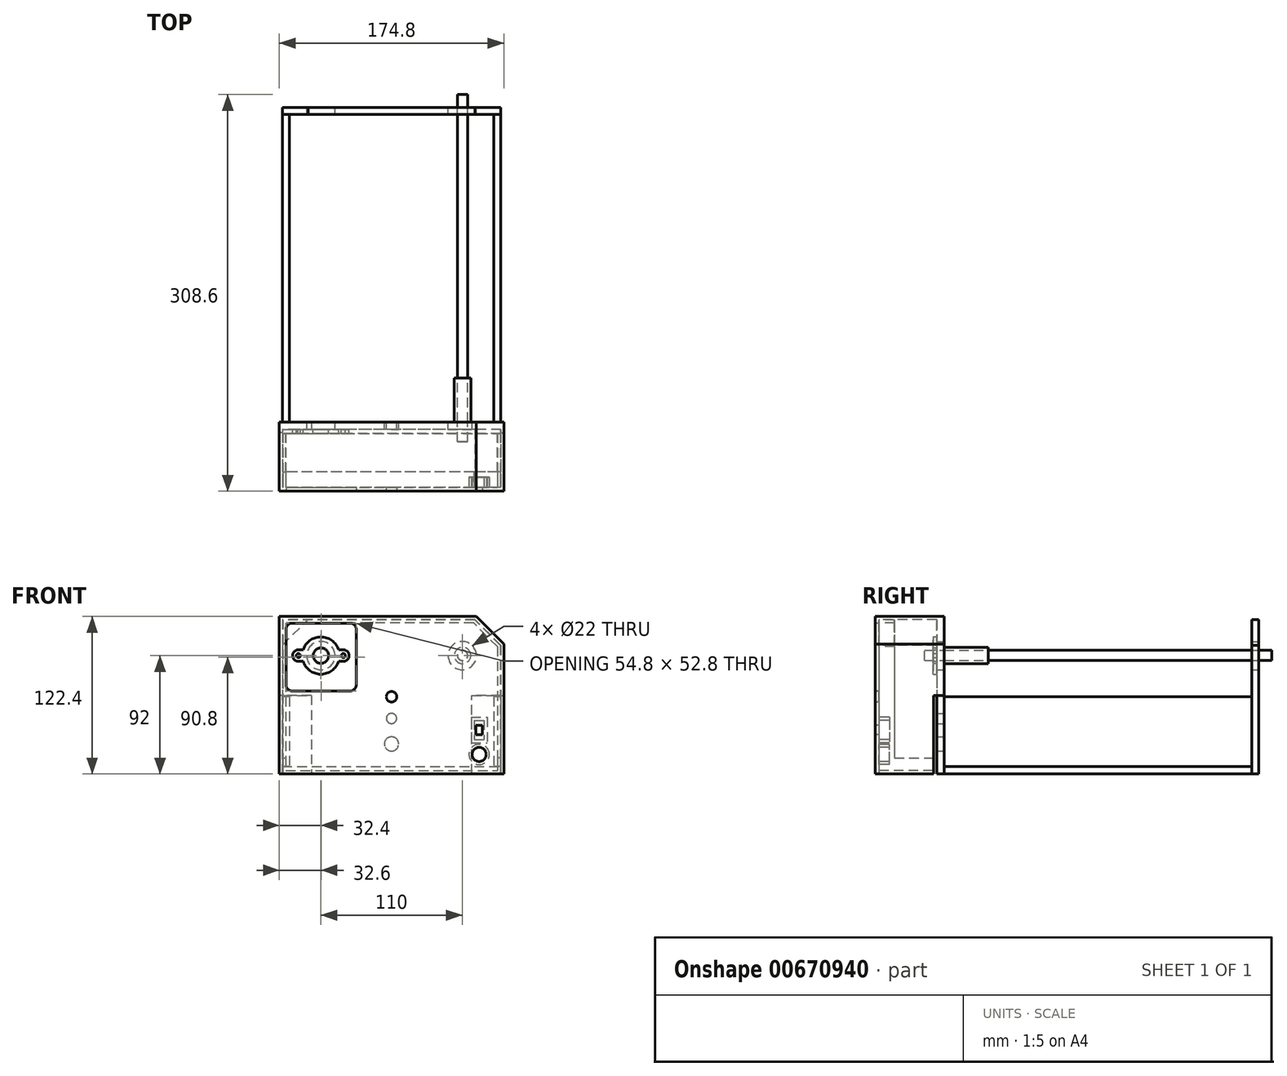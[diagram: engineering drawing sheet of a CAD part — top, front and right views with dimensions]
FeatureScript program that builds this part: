
annotation { "Feature Type Name" : "Feature", "Feature Type Description" : "" }
export const myFeature = defineFeature(function(context is Context, id is Id, definition is map)
    precondition{}
    {
        {
            var Q0;
            Q0=qCreatedBy(makeId("Front.planeOp"),FACE);
            var sketch = newSketch(context, id + "F0", { "sketchPlane" : qUnion([Q0])});
            skLineSegment(sketch, "E0.bottom", {"start": v(85, 60) * mm, "end": v(-85, 60) * mm});
            skLineSegment(sketch, "E0.top", {"start": v(85, -60) * mm, "end": v(-85, -60) * mm});
            skLineSegment(sketch, "E0.left", {"start": v(85, 60) * mm, "end": v(85, -60) * mm});
            skLineSegment(sketch, "E0.right", {"start": v(-85, 60) * mm, "end": v(-85, -60) * mm});
            skPoint(sketch, "E0.middle", {"position": v(0, 0) * mm});
            skLineSegment(sketch, "E1", {"start": v(-85, 32) * mm, "end": v(85, 32) * mm, "construction": true});
            skLineSegment(sketch, "E2", {"start": v(0, 60) * mm, "end": v(0, -60) * mm, "construction": true});
            skLineSegment(sketch, "E3", {"start": v(55, 60) * mm, "end": v(55, -60) * mm, "construction": true});
            skLineSegment(sketch, "E4", {"start": v(-55, 60) * mm, "end": v(-55, -60) * mm, "construction": true});
            skCircle(sketch, "E5", {"center": v(-55, 32) * mm, "radius": 11 * mm});
            skCircle(sketch, "E6", {"center": v(55, 32) * mm, "radius": 11 * mm});
            skSolve(sketch);
        }
        {
            var Q0;
            Q0=makeQuery(id+"F0.imprint","IMPRINT",FACE,{"disambiguationData":[TD([[makeQuery(id+"F0.imprint","IMPRINT",EDGE,{"derivedFrom":sQuery(id+"F0.wireOp",EDGE,"E0.bottom")}),1.0]])]});
            extrude(context, id + "F1", {"entities" : qUnion([Q0]), "depth" : 5.6 * mm, "offsetDistance" : 25 * mm});
        }
        {
            var Q0;
            Q0=makeQuery(id+"F1.opExtrude","SWEPT_EDGE",EDGE,{"disambiguationData":[OSD([sQuery(id+"F0.wireOp",EDGE,"E0.bottom"),sQuery(id+"F0.wireOp",EDGE,"E0.right")])]});
            var Q1;
            Q1=makeQuery(id+"F1.opExtrude","SWEPT_EDGE",EDGE,{"disambiguationData":[OSD([sQuery(id+"F0.wireOp",EDGE,"E0.bottom"),sQuery(id+"F0.wireOp",EDGE,"E0.left")])]});
            chamfer(context, id + "F2", {"entities" : qUnion([Q0, Q1]), "width" : 20 * mm, "tangentPropagation" : true});
        }
        {
            var Q0;
            Q0=makeQuery(id+"F1.opExtrude","SWEPT_BODY",BODY,{"disambiguationData":[OSD([sQuery(id+"F0.wireOp",EDGE,"E0.bottom"),sQuery(id+"F0.wireOp",EDGE,"E0.top"),sQuery(id+"F0.wireOp",EDGE,"E0.left"),sQuery(id+"F0.wireOp",EDGE,"E0.right"),sQuery(id+"F0.wireOp",EDGE,"E5"),sQuery(id+"F0.wireOp",EDGE,"E6")])]});
            transform(context, id + "F3", {"entities" : qUnion([Q0]), "transformType" : TransformType.TRANSLATION_3D, "dx" : 0 * mm, "dy" : 245 * mm, "dz" : 0 * mm, "makeCopy" : true});
        }
        {
            var Q0;
            Q0=qCreatedBy(makeId("Top.planeOp"),FACE);
            var sketch = newSketch(context, id + "F4", { "sketchPlane" : qUnion([Q0])});
            skLineSegment(sketch, "E7.0.0", {"start": v(-85, 0) * mm, "end": v(85, 0) * mm});
            skLineSegment(sketch, "E7.0.1", {"start": v(85, 0) * mm, "end": v(85, -5.6) * mm});
            skLineSegment(sketch, "E7.0.2", {"start": v(85, -5.6) * mm, "end": v(-85, -5.6) * mm});
            skLineSegment(sketch, "E7.0.3", {"start": v(-85, -5.6) * mm, "end": v(-85, 0) * mm});
            skLineSegment(sketch, "E8.0", {"start": v(85, 239.4) * mm, "end": v(-85, 239.4) * mm});
            skLineSegment(sketch, "E9.top", {"start": v(-85, 239.4) * mm, "end": v(85, 239.4) * mm});
            skLineSegment(sketch, "E9.left", {"start": v(-85, 0) * mm, "end": v(-85, 239.4) * mm});
            skLineSegment(sketch, "E9.right", {"start": v(85, 0) * mm, "end": v(85, 239.4) * mm});
            skSolve(sketch);
        }
        {
            var Q0;
            Q0=makeQuery(id+"F4.imprint","IMPRINT",FACE,{"disambiguationData":[TD([[makeQuery(id+"F4.imprint","IMPRINT",EDGE,{"derivedFrom":sQuery(id+"F4.wireOp",EDGE,"E7.0.0")}),1.0]])]});
            extrude(context, id + "F5", {"entities" : qUnion([Q0]), "depth" : 5.6 * mm, "offsetDistance" : 25 * mm});
        }
        {
            var Q0;
            Q0=makeQuery(id+"F5.opExtrude","SWEPT_BODY",BODY,{"disambiguationData":[OSD([sQuery(id+"F4.wireOp",EDGE,"E7.0.0"),sQuery(id+"F4.wireOp",EDGE,"E9.top"),sQuery(id+"F4.wireOp",EDGE,"E9.left"),sQuery(id+"F4.wireOp",EDGE,"E9.right")])]});
            transform(context, id + "F6", {"entities" : qUnion([Q0]), "transformType" : TransformType.TRANSLATION_3D, "dx" : 0 * mm, "dy" : 0 * mm, "dz" : -60 * mm, "makeCopy" : false});
        }
        {
            var Q0;
            Q0=qCreatedBy(makeId("Right.planeOp"),FACE);
            var sketch = newSketch(context, id + "F7", { "sketchPlane" : qUnion([Q0])});
            skLineSegment(sketch, "E10.0", {"start": v(239.4, 40) * mm, "end": v(239.4, -60) * mm});
            skLineSegment(sketch, "E11.0", {"start": v(0, 40) * mm, "end": v(0, -60) * mm});
            skLineSegment(sketch, "E12.bottom", {"start": v(239.4, -54.35) * mm, "end": v(0, -54.35) * mm});
            skLineSegment(sketch, "E12.top", {"start": v(239.4, 0) * mm, "end": v(0, 0) * mm});
            skLineSegment(sketch, "E12.left", {"start": v(239.4, -54.35) * mm, "end": v(239.4, 0) * mm});
            skLineSegment(sketch, "E12.right", {"start": v(0, -54.35) * mm, "end": v(0, 0) * mm});
            skSolve(sketch);
        }
        {
            var Q0;
            Q0=makeQuery(id+"F7.imprint","IMPRINT",FACE,{"disambiguationData":[TD([[makeQuery(id+"F7.imprint","IMPRINT",EDGE,{"derivedFrom":sQuery(id+"F7.wireOp",EDGE,"E12.bottom")}),-1.0]])]});
            extrude(context, id + "F8", {"entities" : qUnion([Q0]), "depth" : 5.6 * mm, "offsetDistance" : 25 * mm});
        }
        {
            var Q0;
            Q0=makeQuery(id+"F8.opExtrude","SWEPT_BODY",BODY,{"disambiguationData":[OSD([sQuery(id+"F7.wireOp",EDGE,"E12.bottom"),sQuery(id+"F7.wireOp",EDGE,"E12.top"),sQuery(id+"F7.wireOp",EDGE,"E12.left"),sQuery(id+"F7.wireOp",EDGE,"E12.right")])]});
            transform(context, id + "F9", {"entities" : qUnion([Q0]), "transformType" : TransformType.TRANSLATION_3D, "dx" : -85 * mm, "dy" : 0 * mm, "dz" : 0 * mm, "makeCopy" : false});
        }
        {
            var Q0;
            Q0=makeQuery(id+"F8.opExtrude","SWEPT_BODY",BODY,{"disambiguationData":[OSD([sQuery(id+"F7.wireOp",EDGE,"E12.bottom"),sQuery(id+"F7.wireOp",EDGE,"E12.top"),sQuery(id+"F7.wireOp",EDGE,"E12.left"),sQuery(id+"F7.wireOp",EDGE,"E12.right")])]});
            transform(context, id + "F10", {"entities" : qUnion([Q0]), "transformType" : TransformType.TRANSLATION_3D, "dx" : 164.4 * mm, "dy" : 0 * mm, "dz" : 0 * mm, "makeCopy" : true});
        }
        {
            var Q0;
            Q0=makeQuery(id+"F1.opExtrude","CAP_FACE",FACE,{"disambiguationData":[OSD([sQuery(id+"F0.wireOp",EDGE,"E0.bottom"),sQuery(id+"F0.wireOp",EDGE,"E0.top"),sQuery(id+"F0.wireOp",EDGE,"E0.left"),sQuery(id+"F0.wireOp",EDGE,"E0.right"),sQuery(id+"F0.wireOp",EDGE,"E5"),sQuery(id+"F0.wireOp",EDGE,"E6")])],"isStart":true});
            var sketch = newSketch(context, id + "F11", { "sketchPlane" : qUnion([Q0])});
            skCircle(sketch, "E13", {"center": v(0, -36.74) * mm, "radius": 5.5 * mm});
            skCircle(sketch, "E14", {"center": v(0, -16.9) * mm, "radius": 4 * mm});
            skSolve(sketch);
        }
        {
            var Q0;
            Q0=makeQuery(id+"F11.imprint","IMPRINT",FACE,{"disambiguationData":[TD([[makeQuery(id+"F11.imprint","IMPRINT",EDGE,{"derivedFrom":sQuery(id+"F11.wireOp",EDGE,"E13")}),1.0]])]});
            var Q1;
            Q1=makeQuery(id+"F11.imprint","IMPRINT",FACE,{"disambiguationData":[TD([[makeQuery(id+"F11.imprint","IMPRINT",EDGE,{"derivedFrom":sQuery(id+"F11.wireOp",EDGE,"E14")}),1.0]])]});
            extrude(context, id + "F12", {"entities" : qUnion([Q0, Q1]), "operationType" : NewBodyOperationType.REMOVE, "oppositeDirection" : true, "depth" : 25 * mm, "offsetDistance" : 25 * mm});
        }
        {
            var Q0;
            Q0=makeQuery(id+"F1.opExtrude","CAP_FACE",FACE,{"disambiguationData":[OSD([sQuery(id+"F0.wireOp",EDGE,"E0.bottom"),sQuery(id+"F0.wireOp",EDGE,"E0.top"),sQuery(id+"F0.wireOp",EDGE,"E0.left"),sQuery(id+"F0.wireOp",EDGE,"E0.right"),sQuery(id+"F0.wireOp",EDGE,"E5"),sQuery(id+"F0.wireOp",EDGE,"E6")])],"isStart":false});
            var sketch = newSketch(context, id + "F13", { "sketchPlane" : qUnion([Q0])});
            skCircle(sketch, "E15", {"center": v(-55, 32) * mm, "radius": 6 * mm});
            skArc(sketch, "E16", {"start": v(-68.78, 27.5) * mm, "mid": v(-55, 17.5) * mm, "end": v(-41.22, 27.5) * mm});
            skLineSegment(sketch, "E17", {"start": v(-55, 32) * mm, "end": v(-37.5, 32) * mm, "construction": true});
            skLineSegment(sketch, "E18", {"start": v(-37.5, 32) * mm, "end": v(-72.5, 32) * mm, "construction": true});
            skCircle(sketch, "E19", {"center": v(-37.5, 32) * mm, "radius": 1.6 * mm});
            skCircle(sketch, "E20", {"center": v(-72.5, 32) * mm, "radius": 1.6 * mm});
            skArc(sketch, "E21", {"start": v(-37.53, 27.5) * mm, "mid": v(-33, 31.94) * mm, "end": v(-37.4, 36.5) * mm});
            skArc(sketch, "E22", {"start": v(-72.29, 36.5) * mm, "mid": v(-77, 32.1) * mm, "end": v(-72.48, 27.5) * mm});
            skLineSegment(sketch, "E23", {"start": v(-37.4, 36.5) * mm, "end": v(-41.24, 36.58) * mm});
            skLineSegment(sketch, "E24", {"start": v(-37.53, 27.5) * mm, "end": v(-41.22, 27.5) * mm});
            skLineSegment(sketch, "E25", {"start": v(-72.71, 36.5) * mm, "end": v(-68.79, 36.5) * mm});
            skLineSegment(sketch, "E26", {"start": v(-72.48, 27.5) * mm, "end": v(-68.78, 27.5) * mm});
            skArc(sketch, "E27.trimOffspring", {"start": v(-41.24, 36.58) * mm, "mid": v(-55.04, 46.5) * mm, "end": v(-68.79, 36.5) * mm});
            skSolve(sketch);
        }
        {
            var Q0;
            Q0=makeQuery(id+"F13.imprint","IMPRINT",FACE,{"disambiguationData":[TD([[makeQuery(id+"F13.imprint","IMPRINT",EDGE,{"derivedFrom":sQuery(id+"F13.wireOp",EDGE,"E15")}),-1.0]])]});
            var Q1;
            Q1=makeQuery(id+"F13.imprint","IMPRINT",FACE,{"disambiguationData":[TD([[makeQuery(id+"F13.imprint","IMPRINT",EDGE,{"derivedFrom":sQuery(id+"F13.wireOp",EDGE,"E16")}),1.0]])]});
            extrude(context, id + "F14", {"entities" : qUnion([Q0, Q1]), "depth" : 3 * mm, "offsetDistance" : 25 * mm});
        }
        {
            var Q0;
            Q0=qCreatedBy(makeId("Front.planeOp"),FACE);
            var sketch = newSketch(context, id + "F15", { "sketchPlane" : qUnion([Q0])});
            skCircle(sketch, "E28", {"center": v(55.27, 32.1) * mm, "radius": 3.92 * mm});
            skSolve(sketch);
        }
        {
            var Q0;
            Q0=makeQuery(id+"F15.imprint","IMPRINT",FACE,{"disambiguationData":[TD([[makeQuery(id+"F15.imprint","IMPRINT",EDGE,{"derivedFrom":sQuery(id+"F15.wireOp",EDGE,"E28")}),1.0]])]});
            extrude(context, id + "F16", {"entities" : qUnion([Q0]), "endBound" : BoundingType.SYMMETRIC, "depth" : 270 * mm, "offsetDistance" : 25 * mm});
        }
        {
            var Q0;
            Q0=makeQuery(id+"F16.opExtrude","SWEPT_BODY",BODY,{"disambiguationData":[OSD([sQuery(id+"F15.wireOp",EDGE,"E28")])]});
            transform(context, id + "F17", {"entities" : qUnion([Q0]), "transformType" : TransformType.TRANSLATION_3D, "dx" : 0 * mm, "dy" : 120 * mm, "dz" : 0 * mm, "makeCopy" : false});
        }
        {
            var Q0;
            Q0=makeQuery(id+"F16.opExtrude","CAP_FACE",FACE,{"disambiguationData":[OSD([sQuery(id+"F15.wireOp",EDGE,"E28")])],"isStart":false});
            var sketch = newSketch(context, id + "F18", { "sketchPlane" : qUnion([Q0])});
            skCircle(sketch, "E29", {"center": v(55.27, 32.1) * mm, "radius": 4 * mm});
            skCircle(sketch, "E30", {"center": v(55.27, 32.1) * mm, "radius": 6.4 * mm});
            skSolve(sketch);
        }
        {
            var Q0;
            Q0=makeQuery(id+"F18.imprint","IMPRINT",FACE,{"disambiguationData":[TD([[makeQuery(id+"F18.imprint","IMPRINT",EDGE,{"derivedFrom":sQuery(id+"F18.wireOp",EDGE,"E29")}),-1.0]])]});
            extrude(context, id + "F19", {"entities" : qUnion([Q0]), "depth" : 34.1 * mm, "offsetDistance" : 25 * mm});
        }
        {
            var Q0;
            Q0=makeQuery(id+"F19.opExtrude","SWEPT_BODY",BODY,{"disambiguationData":[OSD([sQuery(id+"F18.wireOp",EDGE,"E29"),sQuery(id+"F18.wireOp",EDGE,"E30")])]});
            transform(context, id + "F20", {"entities" : qUnion([Q0]), "transformType" : TransformType.TRANSLATION_3D, "dx" : 0 * mm, "dy" : 49.3 * mm, "dz" : 0 * mm, "makeCopy" : false});
        }
        {
            var Q0;
            Q0=makeQuery(id+"F1.opExtrude","CAP_FACE",FACE,{"disambiguationData":[OSD([sQuery(id+"F0.wireOp",EDGE,"E0.bottom"),sQuery(id+"F0.wireOp",EDGE,"E0.top"),sQuery(id+"F0.wireOp",EDGE,"E0.left"),sQuery(id+"F0.wireOp",EDGE,"E0.right"),sQuery(id+"F0.wireOp",EDGE,"E5"),sQuery(id+"F0.wireOp",EDGE,"E6")])],"isStart":false});
            var sketch = newSketch(context, id + "F21", { "sketchPlane" : qUnion([Q0])});
            skLineSegment(sketch, "E31.0", {"start": v(-87.4, 41) * mm, "end": v(-87.4, -60) * mm});
            skLineSegment(sketch, "E31.1", {"start": v(87.4, 41) * mm, "end": v(87.4, -60) * mm});
            skLineSegment(sketch, "E31.2", {"start": v(87.4, 41) * mm, "end": v(66, 62.4) * mm});
            skLineSegment(sketch, "E31.3", {"start": v(66, 62.4) * mm, "end": v(-66, 62.4) * mm});
            skLineSegment(sketch, "E32", {"start": v(-87.4, -60) * mm, "end": v(87.4, -60) * mm});
            skLineSegment(sketch, "E33", {"start": v(-66, 62.4) * mm, "end": v(-87.4, 62.4) * mm});
            skLineSegment(sketch, "E34", {"start": v(-87.4, 41) * mm, "end": v(-87.4, 62.4) * mm});
            skSolve(sketch);
        }
        {
            var Q0;
            {var subQ8=sQuery(id+"F21.wireOp",EDGE,"E31.0");Q0=makeQuery(id+"F21.imprint","IMPRINT",FACE,{"disambiguationData":[TD([[makeQuery(id+"F21.imprint","IMPRINT",EDGE,{"derivedFrom":subQ8}),1.0]])]});}
            extrude(context, id + "F22", {"entities" : qUnion([Q0]), "oppositeDirection" : true, "depth" : 5.6 * mm, "offsetDistance" : 25 * mm});
        }
        {
            var Q0;
            Q0=makeQuery(id+"F22.opExtrude","CAP_FACE",FACE,{"disambiguationData":[OSD([sQuery(id+"F0.wireOp",EDGE,"E0.bottom"),sQuery(id+"F0.wireOp",EDGE,"E0.top"),sQuery(id+"F0.wireOp",EDGE,"E0.left"),sQuery(id+"F0.wireOp",EDGE,"E0.right"),sQuery(id+"F0.wireOp",EDGE,"E5"),sQuery(id+"F0.wireOp",EDGE,"E6"),sQuery(id+"F21.wireOp",EDGE,"E31.0"),sQuery(id+"F21.wireOp",EDGE,"E31.1"),sQuery(id+"F21.wireOp",EDGE,"E31.2"),sQuery(id+"F21.wireOp",EDGE,"E31.3"),sQuery(id+"F21.wireOp",EDGE,"E31.4"),sQuery(id+"F21.wireOp",EDGE,"E32")])],"isStart":true});
            extrude(context, id + "F23", {"entities" : qUnion([Q0]), "operationType" : NewBodyOperationType.ADD, "depth" : 45 * mm, "offsetDistance" : 25 * mm});
        }
        {
            var Q0;
            Q0=makeQuery(id+"F23.opExtrude","CAP_FACE",FACE,{"disambiguationData":[OSD([sQuery(id+"F0.wireOp",EDGE,"E0.bottom"),sQuery(id+"F0.wireOp",EDGE,"E0.top"),sQuery(id+"F0.wireOp",EDGE,"E0.left"),sQuery(id+"F0.wireOp",EDGE,"E0.right"),sQuery(id+"F0.wireOp",EDGE,"E5"),sQuery(id+"F0.wireOp",EDGE,"E6"),sQuery(id+"F21.wireOp",EDGE,"E31.0"),sQuery(id+"F21.wireOp",EDGE,"E31.1"),sQuery(id+"F21.wireOp",EDGE,"E31.2"),sQuery(id+"F21.wireOp",EDGE,"E31.3"),sQuery(id+"F21.wireOp",EDGE,"E32"),sQuery(id+"F21.wireOp",EDGE,"E33"),sQuery(id+"F21.wireOp",EDGE,"E34")])],"isStart":false});
            var sketch = newSketch(context, id + "F24", { "sketchPlane" : qUnion([Q0])});
            skLineSegment(sketch, "E35", {"start": v(-65, 60) * mm, "end": v(-85, 60) * mm});
            skLineSegment(sketch, "E36", {"start": v(-85, 40) * mm, "end": v(-85, 60) * mm});
            skSolve(sketch);
        }
        {
            var Q0;
            Q0=makeQuery(id+"F24.imprint","IMPRINT",FACE,{"disambiguationData":[TD([[makeQuery(id+"F24.imprint","IMPRINT",EDGE,{"derivedFrom":sQuery(id+"F24.wireOp",EDGE,"E35")}),1.0]])]});
            extrude(context, id + "F25", {"entities" : qUnion([Q0]), "operationType" : NewBodyOperationType.REMOVE, "oppositeDirection" : true, "depth" : 45 * mm, "offsetDistance" : 25 * mm});
        }
        {
            var Q0;
            {var subQ0=sQuery(id+"F21.wireOp",EDGE,"E34");var subQ1=sQuery(id+"F21.wireOp",EDGE,"E31.0");Q0=makeQuery(id+"F23.boolean.opBoolean","MERGE",FACE,{"derivedFrom":[makeQuery(id+"F22.opExtrude","SWEPT_FACE",FACE,{"disambiguationData":[OSD([subQ1,subQ0])]}),makeQuery(id+"F23.opExtrude","SWEPT_FACE",FACE,{"disambiguationData":[OSD([subQ1,subQ0])]})]});}
            var sketch = newSketch(context, id + "F26", { "sketchPlane" : qUnion([Q0])});
            skLineSegment(sketch, "E37.bottom", {"start": v(0, -60) * mm, "end": v(8.2, -60) * mm});
            skLineSegment(sketch, "E37.top", {"start": v(0, 1) * mm, "end": v(8.2, 1) * mm});
            skLineSegment(sketch, "E37.left", {"start": v(0, -60) * mm, "end": v(0, 1) * mm});
            skLineSegment(sketch, "E37.right", {"start": v(8.2, -60) * mm, "end": v(8.2, 1) * mm});
            skSolve(sketch);
        }
        {
            var Q0;
            Q0=makeQuery(id+"F26.imprint","IMPRINT",FACE,{"disambiguationData":[TD([[makeQuery(id+"F26.imprint","IMPRINT",EDGE,{"derivedFrom":sQuery(id+"F26.wireOp",EDGE,"E37.bottom")}),1.0]])]});
            extrude(context, id + "F27", {"entities" : qUnion([Q0]), "operationType" : NewBodyOperationType.REMOVE, "oppositeDirection" : true, "depth" : 25 * mm, "offsetDistance" : 25 * mm});
        }
        {
            var Q0;
            {var subQ0=sQuery(id+"F21.wireOp",EDGE,"E31.1");Q0=makeQuery(id+"F23.boolean.opBoolean","MERGE",FACE,{"derivedFrom":[makeQuery(id+"F22.opExtrude","SWEPT_FACE",FACE,{"disambiguationData":[OSD([subQ0])]}),makeQuery(id+"F23.opExtrude","SWEPT_FACE",FACE,{"disambiguationData":[OSD([subQ0])]})]});}
            var sketch = newSketch(context, id + "F28", { "sketchPlane" : qUnion([Q0])});
            skLineSegment(sketch, "E38.bottom", {"start": v(0, -60) * mm, "end": v(-8.2, -60) * mm});
            skLineSegment(sketch, "E38.top", {"start": v(0, 1) * mm, "end": v(-8.2, 1) * mm});
            skLineSegment(sketch, "E38.left", {"start": v(0, -60) * mm, "end": v(0, 1) * mm});
            skLineSegment(sketch, "E38.right", {"start": v(-8.2, -60) * mm, "end": v(-8.2, 1) * mm});
            skSolve(sketch);
        }
        {
            var Q0;
            Q0=makeQuery(id+"F28.imprint","IMPRINT",FACE,{"disambiguationData":[TD([[makeQuery(id+"F28.imprint","IMPRINT",EDGE,{"derivedFrom":sQuery(id+"F28.wireOp",EDGE,"E38.bottom")}),-1.0]])]});
            extrude(context, id + "F29", {"entities" : qUnion([Q0]), "operationType" : NewBodyOperationType.REMOVE, "oppositeDirection" : true, "depth" : 25 * mm, "offsetDistance" : 25 * mm});
        }
        {
            var Q0;
            Q0=makeQuery(id+"F23.opExtrude","CAP_FACE",FACE,{"disambiguationData":[OSD([sQuery(id+"F0.wireOp",EDGE,"E0.bottom"),sQuery(id+"F0.wireOp",EDGE,"E0.top"),sQuery(id+"F0.wireOp",EDGE,"E0.left"),sQuery(id+"F0.wireOp",EDGE,"E0.right"),sQuery(id+"F0.wireOp",EDGE,"E5"),sQuery(id+"F0.wireOp",EDGE,"E6"),sQuery(id+"F21.wireOp",EDGE,"E31.0"),sQuery(id+"F21.wireOp",EDGE,"E31.1"),sQuery(id+"F21.wireOp",EDGE,"E31.2"),sQuery(id+"F21.wireOp",EDGE,"E31.3"),sQuery(id+"F21.wireOp",EDGE,"E32"),sQuery(id+"F21.wireOp",EDGE,"E33"),sQuery(id+"F21.wireOp",EDGE,"E34")])],"isStart":false});
            var sketch = newSketch(context, id + "F30", { "sketchPlane" : qUnion([Q0])});
            skLineSegment(sketch, "E39.0", {"start": v(-84.75, 59.75) * mm, "end": v(-84.75, -60) * mm});
            skLineSegment(sketch, "E39.1", {"start": v(64.9, 59.75) * mm, "end": v(-84.75, 59.75) * mm});
            skLineSegment(sketch, "E39.2", {"start": v(84.75, 39.9) * mm, "end": v(64.9, 59.75) * mm});
            skLineSegment(sketch, "E39.3", {"start": v(84.75, 39.9) * mm, "end": v(84.75, -60) * mm});
            skLineSegment(sketch, "E40.0", {"start": v(-82.35, 57.35) * mm, "end": v(-82.35, -60) * mm});
            skLineSegment(sketch, "E40.1", {"start": v(63.9, 57.35) * mm, "end": v(-82.35, 57.35) * mm});
            skLineSegment(sketch, "E40.2", {"start": v(82.35, 38.9) * mm, "end": v(63.9, 57.35) * mm});
            skLineSegment(sketch, "E40.3", {"start": v(82.35, 38.9) * mm, "end": v(82.35, -60) * mm});
            skLineSegment(sketch, "E41", {"start": v(-82.35, -60) * mm, "end": v(-84.75, -60) * mm});
            skLineSegment(sketch, "E42", {"start": v(82.35, -60) * mm, "end": v(84.75, -60) * mm});
            skSolve(sketch);
        }
        {
            var Q0;
            Q0=makeQuery(id+"F30.imprint","IMPRINT",FACE,{"disambiguationData":[TD([[makeQuery(id+"F30.imprint","IMPRINT",EDGE,{"derivedFrom":sQuery(id+"F30.wireOp",EDGE,"E39.0")}),1.0]])]});
            extrude(context, id + "F31", {"entities" : qUnion([Q0]), "oppositeDirection" : true, "depth" : 12 * mm, "offsetDistance" : 25 * mm});
        }
        {
            var Q0;
            Q0=makeQuery(id+"F31.opExtrude","CAP_FACE",FACE,{"disambiguationData":[OSD([sQuery(id+"F30.wireOp",EDGE,"E39.0"),sQuery(id+"F30.wireOp",EDGE,"E39.1"),sQuery(id+"F30.wireOp",EDGE,"E39.2"),sQuery(id+"F30.wireOp",EDGE,"E39.3"),sQuery(id+"F30.wireOp",EDGE,"E40.0"),sQuery(id+"F30.wireOp",EDGE,"E40.1"),sQuery(id+"F30.wireOp",EDGE,"E40.2"),sQuery(id+"F30.wireOp",EDGE,"E40.3"),sQuery(id+"F30.wireOp",EDGE,"E41"),sQuery(id+"F30.wireOp",EDGE,"E42")])],"isStart":true});
            var sketch = newSketch(context, id + "F32", { "sketchPlane" : qUnion([Q0])});
            skLineSegment(sketch, "E43.0", {"start": v(66, 62.4) * mm, "end": v(-87.4, 62.4) * mm});
            skLineSegment(sketch, "E44.0", {"start": v(-87.4, -60) * mm, "end": v(-87.4, 62.4) * mm});
            skLineSegment(sketch, "E45.0", {"start": v(87.4, 41) * mm, "end": v(66, 62.4) * mm});
            skLineSegment(sketch, "E46.0", {"start": v(87.4, 41) * mm, "end": v(87.4, -60) * mm});
            skLineSegment(sketch, "E47.0", {"start": v(85, -60) * mm, "end": v(-85, -60) * mm});
            skLineSegment(sketch, "E48.0", {"start": v(85, -60) * mm, "end": v(87.4, -60) * mm});
            skLineSegment(sketch, "E49.0", {"start": v(-87.4, -60) * mm, "end": v(-85, -60) * mm});
            skSolve(sketch);
        }
        {
            var Q0;
            {var subQ1=makeQuery(id+"F31.opExtrude","CAP_EDGE",EDGE,{"disambiguationData":[OSD([sQuery(id+"F30.wireOp",EDGE,"E40.0")])],"isStart":true});Q0=makeQuery(id+"F32.imprint","IMPRINT",FACE,{"disambiguationData":[TD([[makeQuery(id+"F32.imprint","IMPRINT",EDGE,{"derivedFrom":subQ1}),1.0]])]});}
            var Q1;
            {var subQ1=makeQuery(id+"F31.opExtrude","CAP_EDGE",EDGE,{"disambiguationData":[OSD([sQuery(id+"F30.wireOp",EDGE,"E39.0")])],"isStart":true});Q1=makeQuery(id+"F32.imprint","IMPRINT",FACE,{"disambiguationData":[TD([[makeQuery(id+"F32.imprint","IMPRINT",EDGE,{"derivedFrom":subQ1}),1.0]])]});}
            var Q2;
            Q2=makeQuery(id+"F32.imprint","IMPRINT",FACE,{"disambiguationData":[TD([[makeQuery(id+"F32.imprint","IMPRINT",EDGE,{"derivedFrom":sQuery(id+"F32.wireOp",EDGE,"E43.0")}),1.0]])]});
            var Q3;
            Q3=sQuery(id+"F32.wireOp",EDGE,"E47.0");
            var Q4;
            Q4=sQuery(id+"F32.wireOp",EDGE,"E48.0");
            var Q5;
            Q5=sQuery(id+"F32.wireOp",EDGE,"E46.0");
            var Q6;
            Q6=sQuery(id+"F32.wireOp",EDGE,"E49.0");
            var Q7;
            Q7=sQuery(id+"F32.wireOp",EDGE,"E44.0");
            var Q8;
            Q8=sQuery(id+"F32.wireOp",EDGE,"E43.0");
            var Q9;
            Q9=sQuery(id+"F32.wireOp",EDGE,"E45.0");
            extrude(context, id + "F33", {"entities" : qUnion([Q0, Q1, Q2]), "operationType" : NewBodyOperationType.ADD, "surfaceEntities" : qUnion([Q3, Q4, Q5, Q6, Q7, Q8, Q9]), "depth" : 3 * mm, "offsetDistance" : 25 * mm});
        }
        {
            var Q0;
            Q0=makeQuery(id+"F33.opExtrude","CAP_FACE",FACE,{"disambiguationData":[OSD([sQuery(id+"F32.wireOp",EDGE,"E43.0"),sQuery(id+"F32.wireOp",EDGE,"E44.0"),sQuery(id+"F32.wireOp",EDGE,"E45.0"),sQuery(id+"F32.wireOp",EDGE,"E46.0"),sQuery(id+"F32.wireOp",EDGE,"E47.0"),sQuery(id+"F32.wireOp",EDGE,"E48.0"),sQuery(id+"F32.wireOp",EDGE,"E49.0")])],"isStart":false});
            var sketch = newSketch(context, id + "F34", { "sketchPlane" : qUnion([Q0])});
            skLineSegment(sketch, "E50.bottom", {"start": v(-87.4, 62.4) * mm, "end": v(-27.4, 62.4) * mm});
            skLineSegment(sketch, "E50.top", {"start": v(-87.4, 4.4) * mm, "end": v(-27.4, 4.4) * mm});
            skLineSegment(sketch, "E50.left", {"start": v(-87.4, 62.4) * mm, "end": v(-87.4, 4.4) * mm});
            skLineSegment(sketch, "E50.right", {"start": v(-27.4, 62.4) * mm, "end": v(-27.4, 4.4) * mm});
            skLineSegment(sketch, "E51", {"start": v(-82.2, 62.4) * mm, "end": v(-82.2, 4.4) * mm});
            skLineSegment(sketch, "E52", {"start": v(-87.4, 57.2) * mm, "end": v(-27.4, 57.2) * mm});
            skSolve(sketch);
        }
        {
            var Q0;
            {var subQ0=sQuery(id+"F34.wireOp",EDGE,"E50.right");var subQ1=sQuery(id+"F34.wireOp",EDGE,"E50.top");var subQ2=makeQuery(id+"F34.imprint","INTERSECT",VERTEX,{"derivedFrom":[subQ1,subQ0]});Q0=makeQuery(id+"F34.imprint","IMPRINT",FACE,{"disambiguationData":[TD([[makeQuery(id+"F34.imprint","IMPRINT",EDGE,{"disambiguationData":[TD([[subQ2,1.0]])],"derivedFrom":subQ1}),1.0]])]});}
            extrude(context, id + "F35", {"entities" : qUnion([Q0]), "operationType" : NewBodyOperationType.REMOVE, "oppositeDirection" : true, "depth" : 25 * mm, "offsetDistance" : 25 * mm});
        }
        {
            var Q0;
            Q0=makeQuery(id+"F35.boolean.opBoolean","COPY",EDGE,{"derivedFrom":makeQuery(id+"F35.opExtrude","SWEPT_EDGE",EDGE,{"disambiguationData":[OSD([sQuery(id+"F34.wireOp",EDGE,"E50.top"),sQuery(id+"F34.wireOp",EDGE,"E50.right")])]})});
            var Q1;
            Q1=makeQuery(id+"F35.boolean.opBoolean","COPY",EDGE,{"derivedFrom":makeQuery(id+"F35.opExtrude","SWEPT_EDGE",EDGE,{"disambiguationData":[OSD([sQuery(id+"F34.wireOp",EDGE,"E50.top"),sQuery(id+"F34.wireOp",EDGE,"E51")])]})});
            var Q2;
            Q2=makeQuery(id+"F35.boolean.opBoolean","COPY",EDGE,{"derivedFrom":makeQuery(id+"F35.opExtrude","SWEPT_EDGE",EDGE,{"disambiguationData":[OSD([sQuery(id+"F34.wireOp",EDGE,"E50.right"),sQuery(id+"F34.wireOp",EDGE,"E52")])]})});
            var Q3;
            Q3=makeQuery(id+"F35.boolean.opBoolean","COPY",EDGE,{"derivedFrom":makeQuery(id+"F35.opExtrude","SWEPT_EDGE",EDGE,{"disambiguationData":[OSD([sQuery(id+"F34.wireOp",EDGE,"E51"),sQuery(id+"F34.wireOp",EDGE,"E52")])]})});
            fillet(context, id + "F36", {"entities" : qUnion([Q0, Q1, Q2, Q3]), "radius" : 5 * mm, "tangentPropagation" : true, "allowEdgeOverflow" : false});
        }
        {
            var Q0;
            {var subQ7=makeQuery(id+"F33.opExtrude","CAP_EDGE",EDGE,{"disambiguationData":[OSD([sQuery(id+"F32.wireOp",EDGE,"E45.0")])],"isStart":false});Q0=makeQuery(id+"F34.imprint","IMPRINT",FACE,{"disambiguationData":[TD([[makeQuery(id+"F34.imprint","IMPRINT",EDGE,{"derivedFrom":subQ7}),1.0]])]});}
            var sketch = newSketch(context, id + "F37", { "sketchPlane" : qUnion([Q0])});
            skCircle(sketch, "E53", {"center": v(0, 0) * mm, "radius": 4.1 * mm});
            skCircle(sketch, "E54", {"center": v(68.19, -44.93) * mm, "radius": 5.5 * mm});
            skLineSegment(sketch, "E55.bottom", {"start": v(70.69, -22.4) * mm, "end": v(65.69, -22.4) * mm});
            skLineSegment(sketch, "E55.top", {"start": v(70.69, -29.4) * mm, "end": v(65.69, -29.4) * mm});
            skLineSegment(sketch, "E55.left", {"start": v(70.69, -22.4) * mm, "end": v(70.69, -29.4) * mm});
            skLineSegment(sketch, "E55.right", {"start": v(65.69, -22.4) * mm, "end": v(65.69, -29.4) * mm});
            skPoint(sketch, "E55.middle", {"position": v(68.19, -25.9) * mm});
            skSolve(sketch);
        }
        {
            var Q0;
            Q0=makeQuery(id+"F37.imprint","IMPRINT",FACE,{"disambiguationData":[TD([[makeQuery(id+"F37.imprint","IMPRINT",EDGE,{"derivedFrom":sQuery(id+"F37.wireOp",EDGE,"E55.bottom")}),1.0]])]});
            var Q1;
            Q1=makeQuery(id+"F37.imprint","IMPRINT",FACE,{"disambiguationData":[TD([[makeQuery(id+"F37.imprint","IMPRINT",EDGE,{"derivedFrom":sQuery(id+"F37.wireOp",EDGE,"E53")}),1.0]])]});
            var Q2;
            Q2=makeQuery(id+"F37.imprint","IMPRINT",FACE,{"disambiguationData":[TD([[makeQuery(id+"F37.imprint","IMPRINT",EDGE,{"derivedFrom":sQuery(id+"F37.wireOp",EDGE,"E54")}),1.0]])]});
            extrude(context, id + "F38", {"entities" : qUnion([Q0, Q1, Q2]), "operationType" : NewBodyOperationType.REMOVE, "oppositeDirection" : true, "depth" : 25 * mm, "offsetDistance" : 25 * mm});
        }
        {
            var Q0;
            {var subQ1=makeQuery(id+"F31.opExtrude","CAP_EDGE",EDGE,{"disambiguationData":[OSD([sQuery(id+"F30.wireOp",EDGE,"E40.0")])],"isStart":true});Q0=makeQuery(id+"F32.imprint","IMPRINT",FACE,{"disambiguationData":[TD([[makeQuery(id+"F32.imprint","IMPRINT",EDGE,{"derivedFrom":subQ1}),1.0]])]});}
            var sketch = newSketch(context, id + "F39", { "sketchPlane" : qUnion([Q0])});
            skLineSegment(sketch, "E56.0", {"start": v(70.69, -22.4) * mm, "end": v(65.69, -22.4) * mm});
            skLineSegment(sketch, "E57.0", {"start": v(70.69, -29.4) * mm, "end": v(65.69, -29.4) * mm});
            skLineSegment(sketch, "E58.0", {"start": v(65.69, -22.4) * mm, "end": v(65.69, -29.4) * mm});
            skLineSegment(sketch, "E59.0", {"start": v(70.69, -22.4) * mm, "end": v(70.69, -29.4) * mm});
            skLineSegment(sketch, "E60.bottom", {"start": v(64.44, -18.4) * mm, "end": v(71.94, -18.4) * mm});
            skLineSegment(sketch, "E60.top", {"start": v(64.44, -33.4) * mm, "end": v(71.94, -33.4) * mm});
            skLineSegment(sketch, "E60.left", {"start": v(64.44, -18.4) * mm, "end": v(64.44, -33.4) * mm});
            skLineSegment(sketch, "E60.right", {"start": v(71.94, -18.4) * mm, "end": v(71.94, -33.4) * mm});
            skPoint(sketch, "E60.middle", {"position": v(68.19, -25.9) * mm});
            skPoint(sketch, "E60.middle.positionSnap0", {"position": v(68.19, -22.4) * mm});
            skPoint(sketch, "E60.middle.positionSnap1", {"position": v(70.69, -25.9) * mm});
            skPoint(sketch, "E60.centerSnap0", {"position": v(68.19, -22.4) * mm});
            skPoint(sketch, "E60.centerSnap1", {"position": v(70.69, -25.9) * mm});
            skLineSegment(sketch, "E61.0", {"start": v(62.04, -16) * mm, "end": v(74.34, -16) * mm});
            skLineSegment(sketch, "E61.1", {"start": v(62.04, -16) * mm, "end": v(62.04, -35.8) * mm});
            skLineSegment(sketch, "E61.2", {"start": v(62.04, -35.8) * mm, "end": v(74.34, -35.8) * mm});
            skLineSegment(sketch, "E61.3", {"start": v(74.34, -16) * mm, "end": v(74.34, -35.8) * mm});
            skSolve(sketch);
        }
        {
            var Q0;
            Q0=makeQuery(id+"F39.imprint","IMPRINT",FACE,{"disambiguationData":[TD([[makeQuery(id+"F39.imprint","IMPRINT",EDGE,{"derivedFrom":sQuery(id+"F39.wireOp",EDGE,"E60.bottom")}),1.0]])]});
            extrude(context, id + "F40", {"entities" : qUnion([Q0]), "operationType" : NewBodyOperationType.ADD, "oppositeDirection" : true, "depth" : 8 * mm, "offsetDistance" : 25 * mm});
        }
        {
            var Q0;
            {var subQ1=makeQuery(id+"F31.opExtrude","CAP_EDGE",EDGE,{"disambiguationData":[OSD([sQuery(id+"F30.wireOp",EDGE,"E40.0")])],"isStart":true});Q0=makeQuery(id+"F32.imprint","IMPRINT",FACE,{"disambiguationData":[TD([[makeQuery(id+"F32.imprint","IMPRINT",EDGE,{"derivedFrom":subQ1}),1.0]])]});}
            var sketch = newSketch(context, id + "F41", { "sketchPlane" : qUnion([Q0])});
            skCircle(sketch, "E62.0", {"center": v(68.19, -44.93) * mm, "radius": 7.9 * mm});
            skCircle(sketch, "E63.0", {"center": v(68.19, -44.93) * mm, "radius": 5.5 * mm});
            skSolve(sketch);
        }
        {
            var Q0;
            Q0=makeQuery(id+"F41.imprint","IMPRINT",FACE,{"disambiguationData":[TD([[makeQuery(id+"F41.imprint","IMPRINT",EDGE,{"derivedFrom":sQuery(id+"F41.wireOp",EDGE,"E62.0")}),1.0]])]});
            extrude(context, id + "F42", {"entities" : qUnion([Q0]), "operationType" : NewBodyOperationType.ADD, "oppositeDirection" : true, "depth" : 8 * mm, "offsetDistance" : 25 * mm});
        }
        {
            var Q0;
            {var subQ1=makeQuery(id+"F31.opExtrude","CAP_EDGE",EDGE,{"disambiguationData":[OSD([sQuery(id+"F30.wireOp",EDGE,"E40.0")])],"isStart":true});Q0=makeQuery(id+"F32.imprint","IMPRINT",FACE,{"disambiguationData":[TD([[makeQuery(id+"F32.imprint","IMPRINT",EDGE,{"derivedFrom":subQ1}),1.0]])]});}
            var sketch = newSketch(context, id + "F43", { "sketchPlane" : qUnion([Q0])});
            skLineSegment(sketch, "E64.0", {"start": v(82.35, 38.9) * mm, "end": v(82.35, -60) * mm});
            skLineSegment(sketch, "E65.0", {"start": v(-82.35, 57.35) * mm, "end": v(-82.35, -60) * mm});
            skLineSegment(sketch, "E66", {"start": v(-82.35, -57.6) * mm, "end": v(82.35, -57.6) * mm});
            skSolve(sketch);
        }
        {
            var Q0;
            {var subQ3=sQuery(id+"F43.wireOp",EDGE,"E66");Q0=makeQuery(id+"F43.imprint","IMPRINT",FACE,{"disambiguationData":[TD([[makeQuery(id+"F43.imprint","IMPRINT",EDGE,{"derivedFrom":subQ3}),-1.0]])]});}
            extrude(context, id + "F44", {"entities" : qUnion([Q0]), "operationType" : NewBodyOperationType.ADD, "oppositeDirection" : true, "depth" : 42 * mm, "offsetDistance" : 25 * mm});
        }
        {
            var Q0;
            Q0=makeQuery(id+"F44.opExtrude","SWEPT_FACE",FACE,{"disambiguationData":[OSD([sQuery(id+"F43.wireOp",EDGE,"E65.0")])]});
            extrude(context, id + "F45", {"entities" : qUnion([Q0]), "operationType" : NewBodyOperationType.ADD, "depth" : 2.4 * mm, "offsetDistance" : 25 * mm});
        }
        {
            var Q0;
            Q0=makeQuery(id+"F44.opExtrude","SWEPT_FACE",FACE,{"disambiguationData":[OSD([sQuery(id+"F43.wireOp",EDGE,"E64.0")])]});
            extrude(context, id + "F46", {"entities" : qUnion([Q0]), "operationType" : NewBodyOperationType.ADD, "depth" : 2.4 * mm, "offsetDistance" : 25 * mm});
        }
        {
            var Q0;
            {var subQ0=sQuery(id+"F43.wireOp",EDGE,"E66");Q0=makeQuery(id+"F46.boolean.opBoolean","MERGE",FACE,{"derivedFrom":[makeQuery(id+"F45.boolean.opBoolean","MERGE",FACE,{"derivedFrom":[makeQuery(id+"F44.opExtrude","SWEPT_FACE",FACE,{"disambiguationData":[OSD([subQ0])]}),makeQuery(id+"F45.opExtrude","SWEPT_FACE",FACE,{"disambiguationData":[OSD([sQuery(id+"F43.wireOp",EDGE,"E65.0"),subQ0])]})]}),makeQuery(id+"F46.opExtrude","SWEPT_FACE",FACE,{"disambiguationData":[OSD([sQuery(id+"F43.wireOp",EDGE,"E64.0"),subQ0])]})]});}
            var sketch = newSketch(context, id + "F47", { "sketchPlane" : qUnion([Q0])});
            skLineSegment(sketch, "E67", {"start": v(82.35, -38.6) * mm, "end": v(82.35, -8.6) * mm});
            skLineSegment(sketch, "E68", {"start": v(-82.35, -38.6) * mm, "end": v(-82.35, -8.6) * mm});
            skSolve(sketch);
        }
        {
            var Q0;
            {var subQ0=sQuery(id+"F47.wireOp",EDGE,"E68");Q0=makeQuery(id+"F47.imprint","IMPRINT",FACE,{"disambiguationData":[TD([[makeQuery(id+"F47.imprint","IMPRINT",EDGE,{"derivedFrom":subQ0}),1.0]])]});}
            var Q1;
            {var subQ0=sQuery(id+"F47.wireOp",EDGE,"E67");Q1=makeQuery(id+"F47.imprint","IMPRINT",FACE,{"disambiguationData":[TD([[makeQuery(id+"F47.imprint","IMPRINT",EDGE,{"derivedFrom":subQ0}),-1.0]])]});}
            extrude(context, id + "F48", {"entities" : qUnion([Q0, Q1]), "operationType" : NewBodyOperationType.ADD, "depth" : 10 * mm, "offsetDistance" : 25 * mm});
        }
    });
